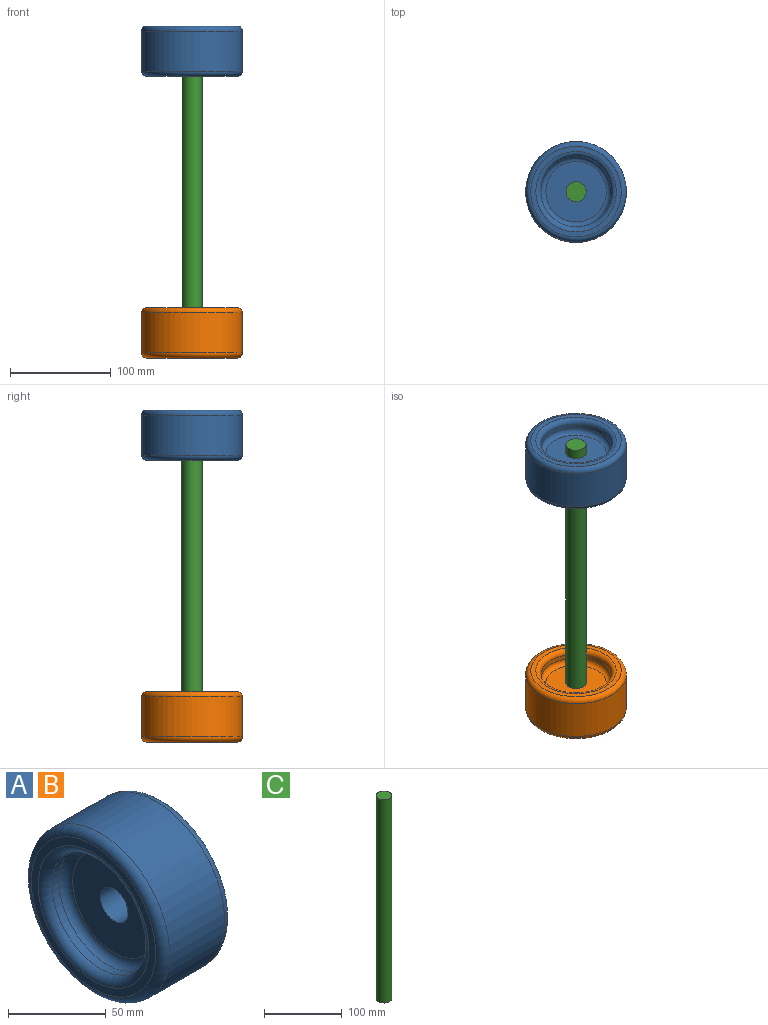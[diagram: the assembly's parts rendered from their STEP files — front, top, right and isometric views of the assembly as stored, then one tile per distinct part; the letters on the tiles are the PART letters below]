
ASSEMBLY  parts=3 mates=2
PART A: 28 faces, bbox 50x108.2x108.2 mm
  f0: plane 60x60mm, normal (1,0,0), area 2513.3mm2, adj f1,f13
  f1: torus R=30mm, axis (-1,0,0), area 1637.5mm2, adj f0,f2
  f2: cylinder r=35mm len=70mm, axis (-1,0,0), area 1099.6mm2, adj f1,f3
  f3: torus R=40mm, axis (-1,0,0), area 1816.8mm2, adj f2,f4
  f4: plane 90x90mm, normal (1,0,0), area 1335.2mm2, adj f3,f5
  f5: torus R=45mm, axis (-1,0,0), area 2377.7mm2, adj f4,f6
  f6: cylinder r=50mm len=100mm, axis (-1,0,0), area 12566.4mm2, adj f5,f7
  f7: torus R=45mm, axis (-1,0,0), area 2377.7mm2, adj f6,f8
  f8: plane 90x90mm, normal (-1,0,0), area 1335.2mm2, adj f7,f9
  f9: torus R=40mm, axis (-1,0,0), area 1816.8mm2, adj f8,f10
  f10: cylinder r=35mm len=70mm, axis (-1,0,0), area 1099.6mm2, adj f9,f11
  f11: torus R=30mm, axis (-1,0,0), area 1637.5mm2, adj f10,f12
  f12: plane 60x60mm, normal (-1,0,0), area 2513.3mm2, adj f11,f13
  f13: cylinder r=10mm len=20mm, axis (1,0,0), area 1256.6mm2, adj f0,f12
  f14: plane 60x60mm, normal (-1,0,0), area 2375mm2, adj f15,f27
  f15: torus R=30mm, axis (-1,0,0), area 2380.5mm2, adj f14,f16
  f16: cylinder r=37mm len=74mm, axis (-1,0,0), area 1162.4mm2, adj f15,f17
  f17: torus R=40mm, axis (-1,0,0), area 1127.8mm2, adj f16,f18
  f18: plane 90x90mm, normal (-1,0,0), area 1335.2mm2, adj f17,f19
  f19: torus R=45mm, axis (-1,0,0), area 1388.9mm2, adj f18,f20
  f20: cylinder r=48mm len=96mm, axis (-1,0,0), area 12063.7mm2, adj f19,f21
  f21: torus R=45mm, axis (-1,0,0), area 1388.9mm2, adj f20,f22
  f22: plane 90x90mm, normal (1,0,0), area 1335.2mm2, adj f21,f23
  f23: torus R=40mm, axis (-1,0,0), area 1127.8mm2, adj f22,f24
  f24: cylinder r=37mm len=74mm, axis (-1,0,0), area 1162.4mm2, adj f23,f25
  f25: torus R=30mm, axis (-1,0,0), area 2380.5mm2, adj f24,f26
  f26: plane 60x60mm, normal (1,0,0), area 2375mm2, adj f25,f27
  f27: cylinder r=12mm len=24mm, axis (1,0,0), area 1206.4mm2, adj f14,f26
PART B: same geometry as A
PART C: 3 faces, bbox 20x20x320 mm
  f0: cylinder r=10mm len=320mm, axis (0,0,-1), area 20106.2mm2, adj f1,f2
  f1: plane 20x20mm, normal (0,0,1), area 314.2mm2, adj f0
  f2: plane 20x20mm, normal (0,0,-1), area 314.2mm2, adj f0
PLACE A rot(axis=(0.71,0,-0.71),180deg) t=(-8.5,-6.06,138.27)mm
PLACE B rot(axis=(0,-1,0),90deg) t=(-8.5,-6.06,-141.73)mm
PLACE C t=(-8.5,-6.06,-161.73)mm fixed
MATE fastened A.f13 <-> C.f0  axis (0,0,1) through (-8.5,-6.06,148.27)mm
MATE fastened B.f1 <-> C.f0  axis (0,0,-1) through (-8.5,-6.06,-151.73)mm
